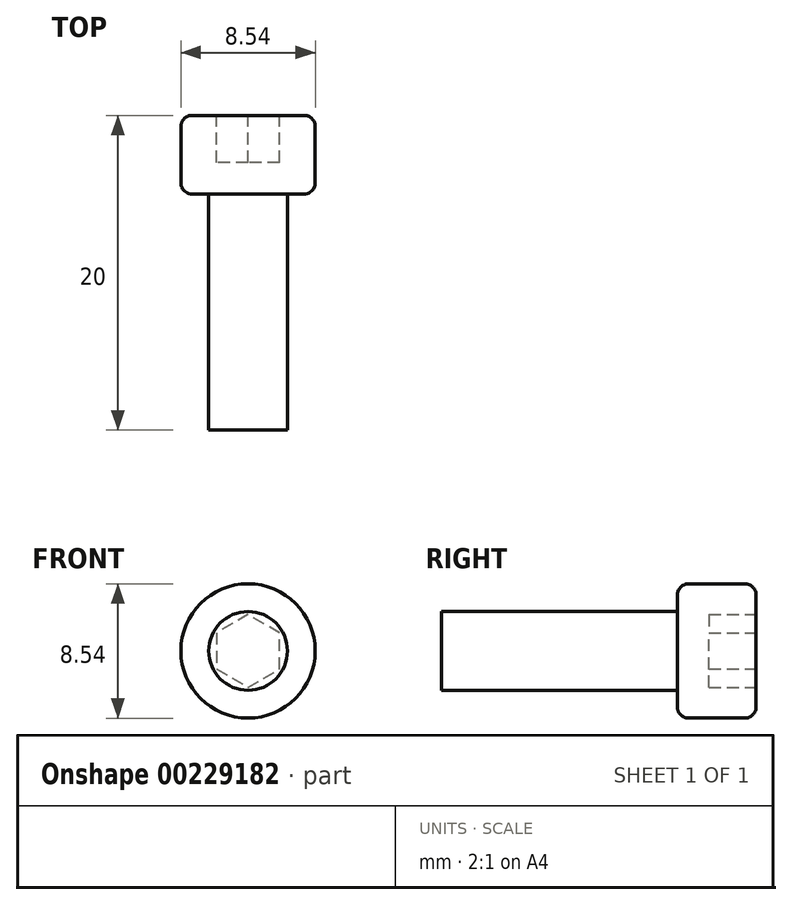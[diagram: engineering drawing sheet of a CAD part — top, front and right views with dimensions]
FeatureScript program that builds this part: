
annotation { "Feature Type Name" : "Feature", "Feature Type Description" : "" }
export const myFeature = defineFeature(function(context is Context, id is Id, definition is map)
    precondition{}
    {
        {
            var Q0;
            Q0=qCreatedBy(makeId("Front.planeOp"),FACE);
            var sketch = newSketch(context, id + "F0", { "sketchPlane" : qUnion([Q0])});
            skCircle(sketch, "E0", {"center": v(0, 0) * mm, "radius": 4.26 * mm});
            skCircle(sketch, "E1", {"center": v(0, 0) * mm, "radius": 2.5 * mm});
            skSolve(sketch);
        }
        {
            var Q0;
            Q0=makeQuery(id+"F0.imprint","IMPRINT",FACE,{"disambiguationData":[TD([[makeQuery(id+"F0.imprint","IMPRINT",EDGE,{"derivedFrom":sQuery(id+"F0.wireOp",EDGE,"E1")}),1.0]])]});
            extrude(context, id + "F1", {"entities" : qUnion([Q0]), "depth" : 15 * mm});
        }
        {
            var Q0;
            Q0=makeQuery(id+"F0.imprint","IMPRINT",FACE,{"disambiguationData":[TD([[makeQuery(id+"F0.imprint","IMPRINT",EDGE,{"derivedFrom":sQuery(id+"F0.wireOp",EDGE,"E0")}),1.0]])]});
            var Q1;
            Q1=makeQuery(id+"F0.imprint","IMPRINT",FACE,{"disambiguationData":[TD([[makeQuery(id+"F0.imprint","IMPRINT",EDGE,{"derivedFrom":sQuery(id+"F0.wireOp",EDGE,"E1")}),1.0]])]});
            extrude(context, id + "F2", {"entities" : qUnion([Q0, Q1]), "operationType" : NewBodyOperationType.ADD, "oppositeDirection" : true, "depth" : 5 * mm});
        }
        {
            var Q0;
            Q0=makeQuery(id+"F2.opExtrude","CAP_FACE",FACE,{"disambiguationData":[OSD([sQuery(id+"F0.wireOp",EDGE,"E0")])],"isStart":false});
            var sketch = newSketch(context, id + "F3", { "sketchPlane" : qUnion([Q0])});
            skCircle(sketch, "E2.cCircle", {"center": v(0, 0) * mm, "radius": 2.3 * mm, "construction": true});
            skLineSegment(sketch, "E2.0", {"start": v(0, 2.3) * mm, "end": v(2, 1.15) * mm});
            skLineSegment(sketch, "E2.1", {"start": v(2, 1.15) * mm, "end": v(2, -1.15) * mm});
            skLineSegment(sketch, "E2.2", {"start": v(2, -1.15) * mm, "end": v(0, -2.3) * mm});
            skLineSegment(sketch, "E2.3", {"start": v(0, -2.3) * mm, "end": v(-2, -1.15) * mm});
            skLineSegment(sketch, "E2.4", {"start": v(-2, -1.15) * mm, "end": v(-2, 1.15) * mm});
            skLineSegment(sketch, "E2.5", {"start": v(-2, 1.15) * mm, "end": v(0, 2.3) * mm});
            skSolve(sketch);
        }
        {
            var Q0;
            Q0=makeQuery(id+"F3.imprint","IMPRINT",FACE,{"disambiguationData":[TD([[makeQuery(id+"F3.imprint","IMPRINT",EDGE,{"derivedFrom":sQuery(id+"F3.wireOp",EDGE,"E2.0")}),-1.0]])]});
            extrude(context, id + "F4", {"entities" : qUnion([Q0]), "operationType" : NewBodyOperationType.REMOVE, "oppositeDirection" : true, "depth" : 3 * mm});
        }
        {
            var Q0;
            Q0=makeQuery(id+"F2.opExtrude","CAP_EDGE",EDGE,{"disambiguationData":[OSD([sQuery(id+"F0.wireOp",EDGE,"E0")])],"isStart":false});
            var Q1;
            Q1=makeQuery(id+"F2.opExtrude","CAP_EDGE",EDGE,{"disambiguationData":[OSD([sQuery(id+"F0.wireOp",EDGE,"E0")])],"isStart":true});
            fillet(context, id + "F5", {"entities" : qUnion([Q0, Q1]), "radius" : 0.7 * mm, "tangentPropagation" : true, "allowEdgeOverflow" : false});
        }
    });
